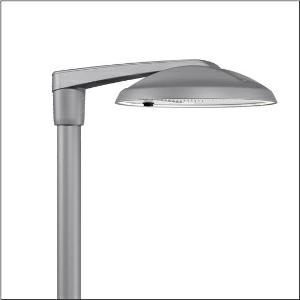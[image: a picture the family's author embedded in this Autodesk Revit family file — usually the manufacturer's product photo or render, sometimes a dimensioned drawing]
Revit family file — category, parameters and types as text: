
# Revit family: dl_50_iq_mini___st1_0a_5xa248d31u08le_5de2
name_source: partatom
category: Lighting Fixtures
units: mm (PartAtom-declared; Revit-internal decimal feet)

## family parameters
Cut with Voids When Loaded = No
Host = Face
Light Source = No
Part Type = Normal
Room Calculation Point = No
Round Connector Dimension = Use Diameter
Shared = No

## types (1)
- --- (1 x LED, 10390 lm, 66 W, 3000K)
    Apparent Load = 66 VA
    CIE Flux Codes = 37 72 97 100 100
    Color Rendering = 70
    Color Temperature = 3000K
    Default Elevation = 1800 mm
    Description = DL 50 iQ mini, mast luminaire, primary light control with lens, of PMMA, primary optical cover: cover, of toughened safety glass, transparent, light distribution: ST1.0a, light emission: direct distribution, primary light characteristic: asymmetric, installation type: post-top, side-entry, LED, High Power LED, rated luminous flux: 10.390lm, luminous efficacy: 157lm/W, light colour: 730, colour temperature: 3000K, control gear: iQ-Street Remote, D4i with power reduction, control: optimised constant luminous flux control (CLO 2.0), Desk-Remote (wireless, voltage-free reading and setting of iQ features in the workshop via application-optimized NFC function/RFID function), Light-Fading, Smart-Wire, Night-Set, Lumen-Switch, Temp-Guard, Auto-Match, Street-Remote, pre-setting: logarithmic dimming characteristic, mains connection: 220..240V, AC, 50/60Hz, connection cable pre-assembled, cable length: 8,5m, start of lifetime: 66W, end of service life: 69W, reduction: 30W, luminaire housing, of diecast aluminium, powder-coated, SITECO metallic grey (DB 702S), inclination adjustable: 0°, 5°, 10° (post-top) | 0°, -5°, -10°, -15° (side-entry), please order mast post-top element or mast side-entry element separately, diameter: 500mm, height: 115mm, post-top: for spigot size d x l = 76 x 100mm; with reducer (optional accessory) 60 x 100mm | side-entry: for spigot size d x l = 60 x 100mm; with reducer (optional accessory) 42 x 100mm, mounting height: 4..6m, Smart Interface below, protection rating (complete): IP66, insulation class (complete): insulation class II (safety insulation), certification: CE, ENEC, ENEC+, VDE, impact resistance: IK08, permissible operating ambient temperature for outdoor applications: -25..+40°C, standard-compliant lighting for roads and squares, packaging unit: 1 piece

Light Distribution: ST1.0a
    Height = 115 mm
    Lamp = 1 x LED
    Lamp Light Flux = 10390 lm
    Lamp Power = 66 W
    Lamp count = 1
    Length = 500 mm
    Luminous efficacy = 157 lm/W
    Manufacturer = Siteco
    ModVariant = No
    Model = 5XA248D31U08LE
    Mounting Place = Pole
    Mounting Type = Pole top
    Number of Poles = 1
    OnlyDefault = Yes
    Power Factor = 1
    Product Name = DL 50 iQ mini | ST1.0a
    Product group = mast luminaire | pylon top
    ProductGroupID = 6100
    Protection Class = Protection class II
    Protection Degree = IP 66
    RLX_Detail_Level = 1
    RLX_Emergency_Light_Flux = 0 lm
    RLX_Emergency_Type = 0
    RLX_Emergency_Type_DB = No
    RlxData = <blob elided: 106377 chars, md5=c7839db0>
    Socket = socket
    Standby Power = 0 W
    System Light Flux = 10390 lm
    System Power = 66 W
    Type Comments = factory setting: luminous flux: 100 % | dim-lin: 254 | 691 mA
    Type Image = l_1296955.jpg
    URL = http://relux.com
    VarID = @adj_074875
    Voltage = 0 V
    Weight = 0.00 kg
    Width = 0 mm  [stored 0 ft]

note: [stored X ft] marks values corroborated as IEEE doubles in the binary element streams (Revit-internal decimal feet)

## geometry (parser evidence)
native form markers: Blend x4, Sweep x11
no freeform markers — native parametric forms only
